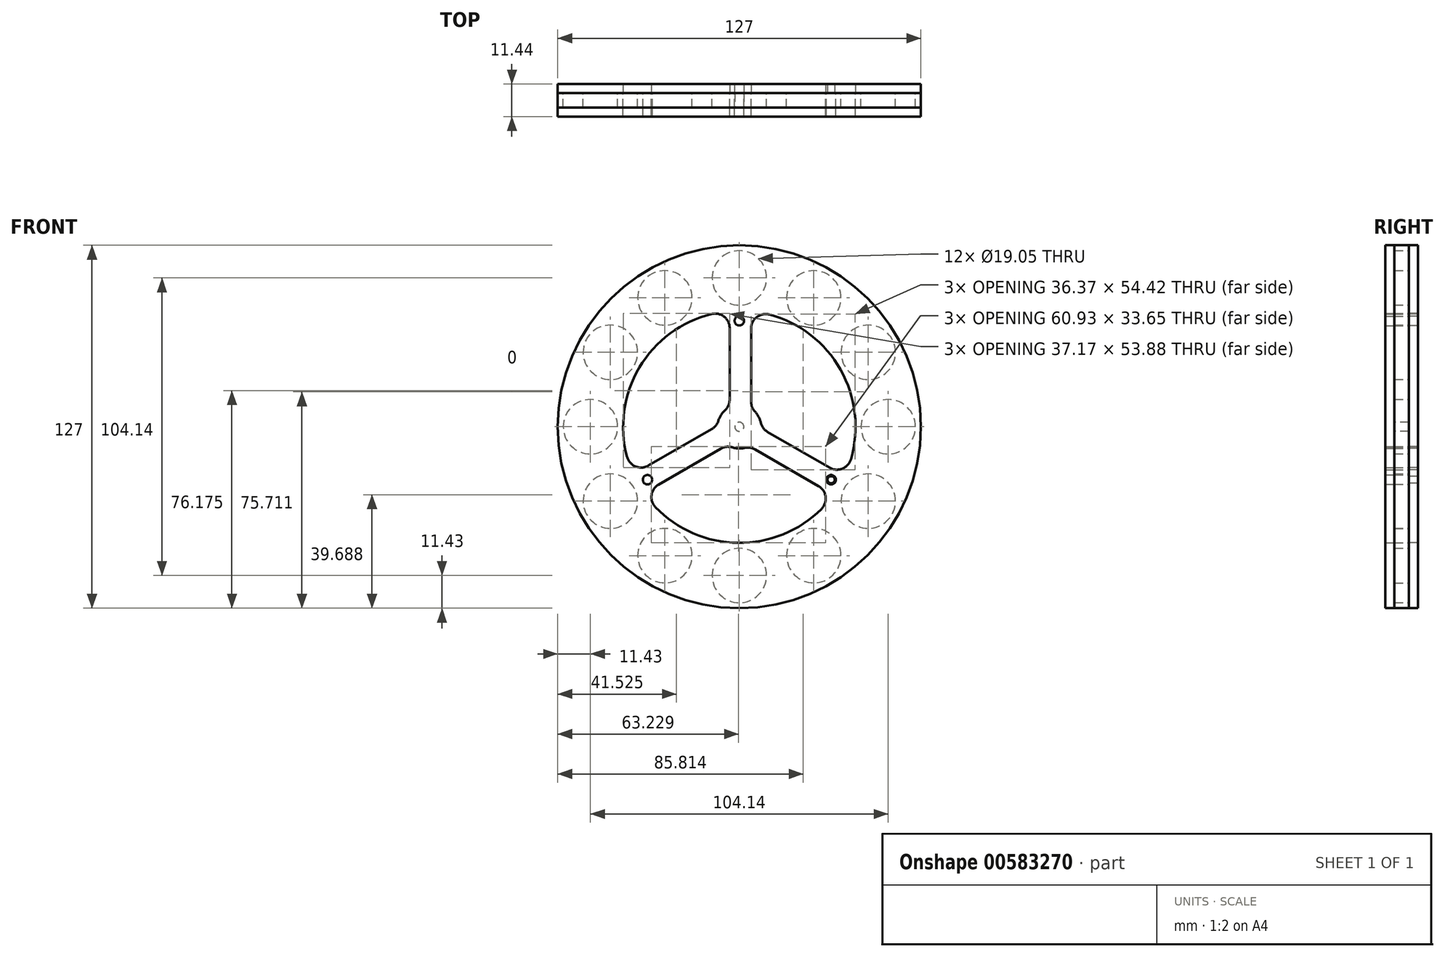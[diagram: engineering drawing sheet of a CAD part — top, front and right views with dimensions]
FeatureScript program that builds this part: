
annotation { "Feature Type Name" : "Feature", "Feature Type Description" : "" }
export const myFeature = defineFeature(function(context is Context, id is Id, definition is map)
    precondition{}
    {
        {
            var Q0;
            Q0=qCreatedBy(makeId("Front.planeOp"),FACE);
            var sketch = newSketch(context, id + "F0", { "sketchPlane" : qUnion([Q0])});
            skCircle(sketch, "E0", {"center": v(0, 0) * mm, "radius": 63.5 * mm});
            skCircle(sketch, "E1.0", {"center": v(0, 0) * mm, "radius": 40.64 * mm});
            skCircle(sketch, "E2", {"center": v(0, 52.07) * mm, "radius": 9.53 * mm});
            skCircle(sketch, "E3.1.0", {"center": v(-26.03, 45.1) * mm, "radius": 9.53 * mm});
            skCircle(sketch, "E3.2.0", {"center": v(-45.1, 26.03) * mm, "radius": 9.52 * mm});
            skCircle(sketch, "E3.3.0", {"center": v(-52.07, 0) * mm, "radius": 9.53 * mm});
            skCircle(sketch, "E3.4.0", {"center": v(-45.1, -26.03) * mm, "radius": 9.53 * mm});
            skCircle(sketch, "E3.5.0", {"center": v(-26.04, -45.1) * mm, "radius": 9.53 * mm});
            skCircle(sketch, "E3.6.0", {"center": v(0, -52.07) * mm, "radius": 9.53 * mm});
            skCircle(sketch, "E4.1.7.0", {"center": v(26.03, -45.1) * mm, "radius": 9.53 * mm});
            skCircle(sketch, "E4.1.8.0", {"center": v(45.1, -26.04) * mm, "radius": 9.53 * mm});
            skCircle(sketch, "E4.1.9.0", {"center": v(52.07, 0) * mm, "radius": 9.53 * mm});
            skCircle(sketch, "E5.1.10.0", {"center": v(45.1, 26.04) * mm, "radius": 9.53 * mm});
            skCircle(sketch, "E5.1.11.0", {"center": v(26.04, 45.1) * mm, "radius": 9.53 * mm});
            skCircle(sketch, "E6.0", {"center": v(0, 0) * mm, "radius": 7.62 * mm});
            skLineSegment(sketch, "E7", {"start": v(0, 14.42) * mm, "end": v(-3.39, 14.42) * mm});
            skLineSegment(sketch, "E8", {"start": v(-3.39, 6.82) * mm, "end": v(-3.39, 40.5) * mm});
            skLineSegment(sketch, "E9", {"start": v(4.13, 6.4) * mm, "end": v(4.13, 40.43) * mm});
            skLineSegment(sketch, "E10.1.0", {"start": v(-4.22, -6.35) * mm, "end": v(-33.38, -23.18) * mm});
            skLineSegment(sketch, "E10.1.1", {"start": v(-7.61, 0.38) * mm, "end": v(-37.08, -16.64) * mm});
            skLineSegment(sketch, "E10.2.0", {"start": v(7.6, -0.48) * mm, "end": v(36.77, -17.31) * mm});
            skLineSegment(sketch, "E10.2.1", {"start": v(3.48, -6.78) * mm, "end": v(32.95, -23.8) * mm});
            skCircle(sketch, "E11", {"center": v(0, 37.07) * mm, "radius": 1.65 * mm});
            skCircle(sketch, "E12.1.0", {"center": v(-32.1, -18.54) * mm, "radius": 1.65 * mm});
            skCircle(sketch, "E12.2.0", {"center": v(32.1, -18.54) * mm, "radius": 1.65 * mm});
            skSolve(sketch);
        }
        {
            var Q0;
            Q0 = qSketchRegion(id + "F0", true);
            var Q1;
            Q1=makeQuery(id+"F0.imprint","IMPRINT",FACE,{"disambiguationData":[TD([[makeQuery(id+"F0.imprint","IMPRINT",EDGE,{"derivedFrom":sQuery(id+"F0.wireOp",EDGE,"E6.0")}),1.0]])]});
            var Q2;
            {var subQ0=sQuery(id+"F0.wireOp",EDGE,"E10.1.0");Q2=makeQuery(id+"F0.imprint","IMPRINT",FACE,{"disambiguationData":[TD([[makeQuery(id+"F0.imprint","IMPRINT",EDGE,{"derivedFrom":subQ0}),-1.0]])]});}
            var Q3;
            {var subQ0=sQuery(id+"F0.wireOp",EDGE,"E10.2.0");Q3=makeQuery(id+"F0.imprint","IMPRINT",FACE,{"disambiguationData":[TD([[makeQuery(id+"F0.imprint","IMPRINT",EDGE,{"derivedFrom":subQ0}),-1.0]])]});}
            var Q4;
            {var subQ4=sQuery(id+"F0.wireOp",EDGE,"E9");Q4=makeQuery(id+"F0.imprint","IMPRINT",FACE,{"disambiguationData":[TD([[makeQuery(id+"F0.imprint","IMPRINT",EDGE,{"derivedFrom":subQ4}),1.0]])]});}
            extrude(context, id + "F1", {"entities" : qUnion([Q0, Q1, Q2, Q3, Q4]), "depth" : 5.08 * mm, "offsetDistance" : 25.4 * mm});
        }
        {
            var Q0;
            Q0=makeQuery(id+"F1.opExtrude","CAP_FACE",FACE,{"disambiguationData":[OSD([sQuery(id+"F0.wireOp",EDGE,"E0"),sQuery(id+"F0.wireOp",EDGE,"E1.0"),sQuery(id+"F0.wireOp",EDGE,"E2"),sQuery(id+"F0.wireOp",EDGE,"E3.1.0"),sQuery(id+"F0.wireOp",EDGE,"E3.2.0"),sQuery(id+"F0.wireOp",EDGE,"E3.3.0"),sQuery(id+"F0.wireOp",EDGE,"E3.4.0"),sQuery(id+"F0.wireOp",EDGE,"E3.5.0"),sQuery(id+"F0.wireOp",EDGE,"E3.6.0"),sQuery(id+"F0.wireOp",EDGE,"E4.1.7.0"),sQuery(id+"F0.wireOp",EDGE,"E4.1.8.0"),sQuery(id+"F0.wireOp",EDGE,"E4.1.9.0"),sQuery(id+"F0.wireOp",EDGE,"E5.1.10.0"),sQuery(id+"F0.wireOp",EDGE,"E5.1.11.0"),sQuery(id+"F0.wireOp",EDGE,"E6.0"),sQuery(id+"F0.wireOp",EDGE,"E8"),sQuery(id+"F0.wireOp",EDGE,"E9"),sQuery(id+"F0.wireOp",EDGE,"E10.1.0"),sQuery(id+"F0.wireOp",EDGE,"E10.1.1"),sQuery(id+"F0.wireOp",EDGE,"E10.2.0"),sQuery(id+"F0.wireOp",EDGE,"E10.2.1")])],"isStart":false});
            var sketch = newSketch(context, id + "F2", { "sketchPlane" : qUnion([Q0])});
            skCircle(sketch, "E13", {"center": v(0, 0) * mm, "radius": 1.59 * mm});
            skSolve(sketch);
        }
        {
            var Q0;
            Q0=makeQuery(id+"F2.imprint","IMPRINT",FACE,{"disambiguationData":[TD([[makeQuery(id+"F2.imprint","IMPRINT",EDGE,{"derivedFrom":sQuery(id+"F2.wireOp",EDGE,"E13")}),1.0]])]});
            extrude(context, id + "F3", {"entities" : qUnion([Q0]), "operationType" : NewBodyOperationType.REMOVE, "oppositeDirection" : true, "depth" : 25.4 * mm, "offsetDistance" : 25.4 * mm});
        }
        {
            var Q0;
            Q0=makeQuery(id+"F1.opExtrude","SWEPT_EDGE",EDGE,{"disambiguationData":[OSD([sQuery(id+"F0.wireOp",EDGE,"E1.0"),sQuery(id+"F0.wireOp",EDGE,"E10.1.1")])]});
            var Q1;
            Q1=makeQuery(id+"F1.opExtrude","SWEPT_EDGE",EDGE,{"disambiguationData":[OSD([sQuery(id+"F0.wireOp",EDGE,"E1.0"),sQuery(id+"F0.wireOp",EDGE,"E8")])]});
            var Q2;
            Q2=makeQuery(id+"F1.opExtrude","SWEPT_EDGE",EDGE,{"disambiguationData":[OSD([sQuery(id+"F0.wireOp",EDGE,"E6.0"),sQuery(id+"F0.wireOp",EDGE,"E10.1.1")])]});
            var Q3;
            Q3=makeQuery(id+"F1.opExtrude","SWEPT_EDGE",EDGE,{"disambiguationData":[OSD([sQuery(id+"F0.wireOp",EDGE,"E6.0"),sQuery(id+"F0.wireOp",EDGE,"E8")])]});
            var Q4;
            Q4=makeQuery(id+"F1.opExtrude","SWEPT_EDGE",EDGE,{"disambiguationData":[OSD([sQuery(id+"F0.wireOp",EDGE,"E1.0"),sQuery(id+"F0.wireOp",EDGE,"E10.1.0")])]});
            var Q5;
            Q5=makeQuery(id+"F1.opExtrude","SWEPT_EDGE",EDGE,{"disambiguationData":[OSD([sQuery(id+"F0.wireOp",EDGE,"E6.0"),sQuery(id+"F0.wireOp",EDGE,"E10.1.0")])]});
            var Q6;
            Q6=makeQuery(id+"F1.opExtrude","SWEPT_EDGE",EDGE,{"disambiguationData":[OSD([sQuery(id+"F0.wireOp",EDGE,"E6.0"),sQuery(id+"F0.wireOp",EDGE,"E10.2.1")])]});
            var Q7;
            Q7=makeQuery(id+"F1.opExtrude","SWEPT_EDGE",EDGE,{"disambiguationData":[OSD([sQuery(id+"F0.wireOp",EDGE,"E1.0"),sQuery(id+"F0.wireOp",EDGE,"E10.2.1")])]});
            var Q8;
            Q8=makeQuery(id+"F1.opExtrude","SWEPT_EDGE",EDGE,{"disambiguationData":[OSD([sQuery(id+"F0.wireOp",EDGE,"E1.0"),sQuery(id+"F0.wireOp",EDGE,"E10.2.0")])]});
            var Q9;
            Q9=makeQuery(id+"F1.opExtrude","SWEPT_EDGE",EDGE,{"disambiguationData":[OSD([sQuery(id+"F0.wireOp",EDGE,"E6.0"),sQuery(id+"F0.wireOp",EDGE,"E9")])]});
            var Q10;
            Q10=makeQuery(id+"F1.opExtrude","SWEPT_EDGE",EDGE,{"disambiguationData":[OSD([sQuery(id+"F0.wireOp",EDGE,"E6.0"),sQuery(id+"F0.wireOp",EDGE,"E10.2.0")])]});
            var Q11;
            Q11=makeQuery(id+"F1.opExtrude","SWEPT_EDGE",EDGE,{"disambiguationData":[OSD([sQuery(id+"F0.wireOp",EDGE,"E1.0"),sQuery(id+"F0.wireOp",EDGE,"E9")])]});
            fillet(context, id + "F4", {"entities" : qUnion([Q0, Q1, Q2, Q3, Q4, Q5, Q6, Q7, Q8, Q9, Q10, Q11]), "radius" : 5.08 * mm, "tangentPropagation" : true, "allowEdgeOverflow" : false});
        }
        {
            var Q0;
            Q0=makeQuery(id+"F1.opExtrude","CAP_FACE",FACE,{"disambiguationData":[OSD([sQuery(id+"F0.wireOp",EDGE,"E0"),sQuery(id+"F0.wireOp",EDGE,"E1.0"),sQuery(id+"F0.wireOp",EDGE,"E2"),sQuery(id+"F0.wireOp",EDGE,"E3.1.0"),sQuery(id+"F0.wireOp",EDGE,"E3.2.0"),sQuery(id+"F0.wireOp",EDGE,"E3.3.0"),sQuery(id+"F0.wireOp",EDGE,"E3.4.0"),sQuery(id+"F0.wireOp",EDGE,"E3.5.0"),sQuery(id+"F0.wireOp",EDGE,"E3.6.0"),sQuery(id+"F0.wireOp",EDGE,"E4.1.7.0"),sQuery(id+"F0.wireOp",EDGE,"E4.1.8.0"),sQuery(id+"F0.wireOp",EDGE,"E4.1.9.0"),sQuery(id+"F0.wireOp",EDGE,"E5.1.10.0"),sQuery(id+"F0.wireOp",EDGE,"E5.1.11.0"),sQuery(id+"F0.wireOp",EDGE,"E6.0"),sQuery(id+"F0.wireOp",EDGE,"E8"),sQuery(id+"F0.wireOp",EDGE,"E9"),sQuery(id+"F0.wireOp",EDGE,"E10.1.0"),sQuery(id+"F0.wireOp",EDGE,"E10.1.1"),sQuery(id+"F0.wireOp",EDGE,"E10.2.0"),sQuery(id+"F0.wireOp",EDGE,"E10.2.1")])],"isStart":false});
            var sketch = newSketch(context, id + "F5", { "sketchPlane" : qUnion([Q0])});
            skCircle(sketch, "E14.0", {"center": v(0, 0) * mm, "radius": 63.5 * mm});
            skArc(sketch, "E15.0", {"start": v(-9.68, 39.47) * mm, "mid": v(-34.97, 20.7) * mm, "end": v(-39.26, -10.5) * mm});
            skPoint(sketch, "E16.0", {"position": v(-36.3, -13.89) * mm});
            skArc(sketch, "E17.0", {"start": v(-31.81, -13.6) * mm, "mid": v(-36.3, -13.89) * mm, "end": v(-39.26, -10.5) * mm});
            skLineSegment(sketch, "E18.0", {"start": v(-9.64, -0.8) * mm, "end": v(-31.81, -13.6) * mm});
            skArc(sketch, "E19.0", {"start": v(-7.3, 2.16) * mm, "mid": v(-8.19, 0.46) * mm, "end": v(-9.64, -0.8) * mm});
            skArc(sketch, "E20.0", {"start": v(-5.08, 5.68) * mm, "mid": v(-6.44, 4.08) * mm, "end": v(-7.3, 2.16) * mm});
            skArc(sketch, "E21.0", {"start": v(-3.39, 9.46) * mm, "mid": v(-3.83, 7.4) * mm, "end": v(-5.08, 5.68) * mm});
            skLineSegment(sketch, "E22.0", {"start": v(-3.39, 9.46) * mm, "end": v(-3.39, 34.54) * mm});
            skArc(sketch, "E23.0", {"start": v(-9.68, 39.47) * mm, "mid": v(-5.33, 38.53) * mm, "end": v(-3.39, 34.54) * mm});
            skCircle(sketch, "E24.0", {"center": v(0, 37.07) * mm, "radius": 1.65 * mm});
            skCircle(sketch, "E25.0", {"center": v(-32.1, -18.54) * mm, "radius": 1.65 * mm});
            skCircle(sketch, "E26.0", {"center": v(32.1, -18.54) * mm, "radius": 1.65 * mm});
            skLineSegment(sketch, "E27.0", {"start": v(9.9, -1.8) * mm, "end": v(31.6, -14.33) * mm});
            skArc(sketch, "E28.0", {"start": v(9.9, -1.8) * mm, "mid": v(8.32, -0.38) * mm, "end": v(7.46, 1.56) * mm});
            skArc(sketch, "E29.0", {"start": v(7.46, 1.56) * mm, "mid": v(6.75, 3.54) * mm, "end": v(5.53, 5.25) * mm});
            skArc(sketch, "E30.0", {"start": v(5.53, 5.25) * mm, "mid": v(4.5, 6.86) * mm, "end": v(4.13, 8.74) * mm});
            skLineSegment(sketch, "E31.0", {"start": v(4.13, 8.74) * mm, "end": v(4.13, 34.35) * mm});
            skArc(sketch, "E32.0", {"start": v(4.13, 34.35) * mm, "mid": v(6.12, 38.38) * mm, "end": v(10.53, 39.25) * mm});
            skArc(sketch, "E33.0", {"start": v(39.02, -11.35) * mm, "mid": v(35.41, 19.94) * mm, "end": v(10.53, 39.25) * mm});
            skArc(sketch, "E34.0", {"start": v(39.02, -11.35) * mm, "mid": v(36.04, -14.65) * mm, "end": v(31.6, -14.33) * mm});
            skLineSegment(sketch, "E35.0", {"start": v(5.5, -7.95) * mm, "end": v(27.68, -20.75) * mm});
            skArc(sketch, "E36.0", {"start": v(1.78, -7.4) * mm, "mid": v(3.7, -7.32) * mm, "end": v(5.5, -7.95) * mm});
            skArc(sketch, "E37.0", {"start": v(-2.38, -7.24) * mm, "mid": v(-0.31, -7.61) * mm, "end": v(1.78, -7.4) * mm});
            skArc(sketch, "E38.0", {"start": v(-6.5, -7.67) * mm, "mid": v(-4.48, -7.01) * mm, "end": v(-2.38, -7.24) * mm});
            skLineSegment(sketch, "E39.0", {"start": v(-6.5, -7.67) * mm, "end": v(-28.22, -20.2) * mm});
            skArc(sketch, "E40.0", {"start": v(-29.34, -28.12) * mm, "mid": v(-30.7, -23.89) * mm, "end": v(-28.22, -20.2) * mm});
            skArc(sketch, "E41.0", {"start": v(-29.34, -28.12) * mm, "mid": v(-0.44, -40.64) * mm, "end": v(28.73, -28.74) * mm});
            skArc(sketch, "E42.0", {"start": v(27.68, -20.75) * mm, "mid": v(30.18, -24.49) * mm, "end": v(28.73, -28.74) * mm});
            skSolve(sketch);
        }
        {
            var Q0;
            Q0 = qSketchRegion(id + "F5", true);
            extrude(context, id + "F6", {"entities" : qUnion([Q0]), "depth" : 3.17 * mm, "offsetDistance" : 25.4 * mm});
        }
        {
            var Q0;
            Q0=makeQuery(id+"F1.opExtrude","CAP_FACE",FACE,{"disambiguationData":[OSD([sQuery(id+"F0.wireOp",EDGE,"E0"),sQuery(id+"F0.wireOp",EDGE,"E1.0"),sQuery(id+"F0.wireOp",EDGE,"E2"),sQuery(id+"F0.wireOp",EDGE,"E3.1.0"),sQuery(id+"F0.wireOp",EDGE,"E3.2.0"),sQuery(id+"F0.wireOp",EDGE,"E3.3.0"),sQuery(id+"F0.wireOp",EDGE,"E3.4.0"),sQuery(id+"F0.wireOp",EDGE,"E3.5.0"),sQuery(id+"F0.wireOp",EDGE,"E3.6.0"),sQuery(id+"F0.wireOp",EDGE,"E4.1.7.0"),sQuery(id+"F0.wireOp",EDGE,"E4.1.8.0"),sQuery(id+"F0.wireOp",EDGE,"E4.1.9.0"),sQuery(id+"F0.wireOp",EDGE,"E5.1.10.0"),sQuery(id+"F0.wireOp",EDGE,"E5.1.11.0"),sQuery(id+"F0.wireOp",EDGE,"E6.0"),sQuery(id+"F0.wireOp",EDGE,"E8"),sQuery(id+"F0.wireOp",EDGE,"E9"),sQuery(id+"F0.wireOp",EDGE,"E10.1.0"),sQuery(id+"F0.wireOp",EDGE,"E10.1.1"),sQuery(id+"F0.wireOp",EDGE,"E10.2.0"),sQuery(id+"F0.wireOp",EDGE,"E10.2.1"),sQuery(id+"F0.wireOp",EDGE,"E11"),sQuery(id+"F0.wireOp",EDGE,"E12.1.0"),sQuery(id+"F0.wireOp",EDGE,"E12.2.0")])],"isStart":true});
            var sketch = newSketch(context, id + "F7", { "sketchPlane" : qUnion([Q0])});
            skCircle(sketch, "E43.0", {"center": v(0, 0) * mm, "radius": 63.5 * mm});
            skCircle(sketch, "E44.0", {"center": v(-32.1, -18.54) * mm, "radius": 1.65 * mm, "construction": true});
            skCircle(sketch, "E45", {"center": v(-32.1, -18.54) * mm, "radius": 1.25 * mm});
            skLineSegment(sketch, "E46.0", {"start": v(-4.13, 8.74) * mm, "end": v(-4.13, 34.35) * mm});
            skArc(sketch, "E47.0", {"start": v(-4.13, 8.74) * mm, "mid": v(-4.5, 6.86) * mm, "end": v(-5.53, 5.25) * mm});
            skArc(sketch, "E48.0", {"start": v(-7.46, 1.56) * mm, "mid": v(-6.75, 3.54) * mm, "end": v(-5.53, 5.25) * mm});
            skArc(sketch, "E49.0", {"start": v(-7.46, 1.56) * mm, "mid": v(-8.32, -0.38) * mm, "end": v(-9.9, -1.8) * mm});
            skLineSegment(sketch, "E50.0", {"start": v(-9.9, -1.8) * mm, "end": v(-31.6, -14.33) * mm});
            skArc(sketch, "E51.0", {"start": v(-39.02, -11.35) * mm, "mid": v(-35.41, 19.94) * mm, "end": v(-10.53, 39.25) * mm});
            skArc(sketch, "E52.0", {"start": v(-31.6, -14.33) * mm, "mid": v(-36.04, -14.65) * mm, "end": v(-39.02, -11.35) * mm});
            skArc(sketch, "E53.0", {"start": v(-10.53, 39.25) * mm, "mid": v(-6.12, 38.38) * mm, "end": v(-4.13, 34.35) * mm});
            skLineSegment(sketch, "E54.0", {"start": v(-5.5, -7.95) * mm, "end": v(-27.68, -20.75) * mm});
            skArc(sketch, "E55.0", {"start": v(-5.5, -7.95) * mm, "mid": v(-3.7, -7.32) * mm, "end": v(-1.78, -7.4) * mm});
            skArc(sketch, "E56.0", {"start": v(2.38, -7.24) * mm, "mid": v(0.31, -7.61) * mm, "end": v(-1.78, -7.4) * mm});
            skArc(sketch, "E57.0", {"start": v(2.38, -7.24) * mm, "mid": v(4.48, -7.01) * mm, "end": v(6.5, -7.67) * mm});
            skLineSegment(sketch, "E58.0", {"start": v(6.5, -7.67) * mm, "end": v(28.22, -20.2) * mm});
            skArc(sketch, "E59.0", {"start": v(-28.73, -28.74) * mm, "mid": v(-30.18, -24.49) * mm, "end": v(-27.68, -20.75) * mm});
            skArc(sketch, "E60.0", {"start": v(29.34, -28.12) * mm, "mid": v(0.44, -40.64) * mm, "end": v(-28.73, -28.74) * mm});
            skArc(sketch, "E61.0", {"start": v(28.22, -20.2) * mm, "mid": v(30.7, -23.89) * mm, "end": v(29.34, -28.12) * mm});
            skLineSegment(sketch, "E62.0", {"start": v(3.39, 9.46) * mm, "end": v(3.39, 34.54) * mm});
            skLineSegment(sketch, "E63.0", {"start": v(9.64, -0.8) * mm, "end": v(31.81, -13.6) * mm});
            skArc(sketch, "E64.0", {"start": v(9.64, -0.8) * mm, "mid": v(8.19, 0.46) * mm, "end": v(7.3, 2.16) * mm});
            skArc(sketch, "E65.0", {"start": v(5.08, 5.68) * mm, "mid": v(6.44, 4.08) * mm, "end": v(7.3, 2.16) * mm});
            skArc(sketch, "E66.0", {"start": v(5.08, 5.68) * mm, "mid": v(3.83, 7.4) * mm, "end": v(3.39, 9.46) * mm});
            skArc(sketch, "E67.0", {"start": v(3.39, 34.54) * mm, "mid": v(5.33, 38.53) * mm, "end": v(9.68, 39.47) * mm});
            skArc(sketch, "E68.0", {"start": v(9.68, 39.47) * mm, "mid": v(34.97, 20.7) * mm, "end": v(39.26, -10.5) * mm});
            skArc(sketch, "E69.0", {"start": v(39.26, -10.5) * mm, "mid": v(36.3, -13.89) * mm, "end": v(31.81, -13.6) * mm});
            skCircle(sketch, "E70.0", {"center": v(0, 37.07) * mm, "radius": 1.65 * mm});
            skSolve(sketch);
        }
        {
            var Q0;
            Q0 = qSketchRegion(id + "F7", true);
            extrude(context, id + "F8", {"entities" : qUnion([Q0]), "depth" : 3.17 * mm, "offsetDistance" : 25.4 * mm});
        }
    });
